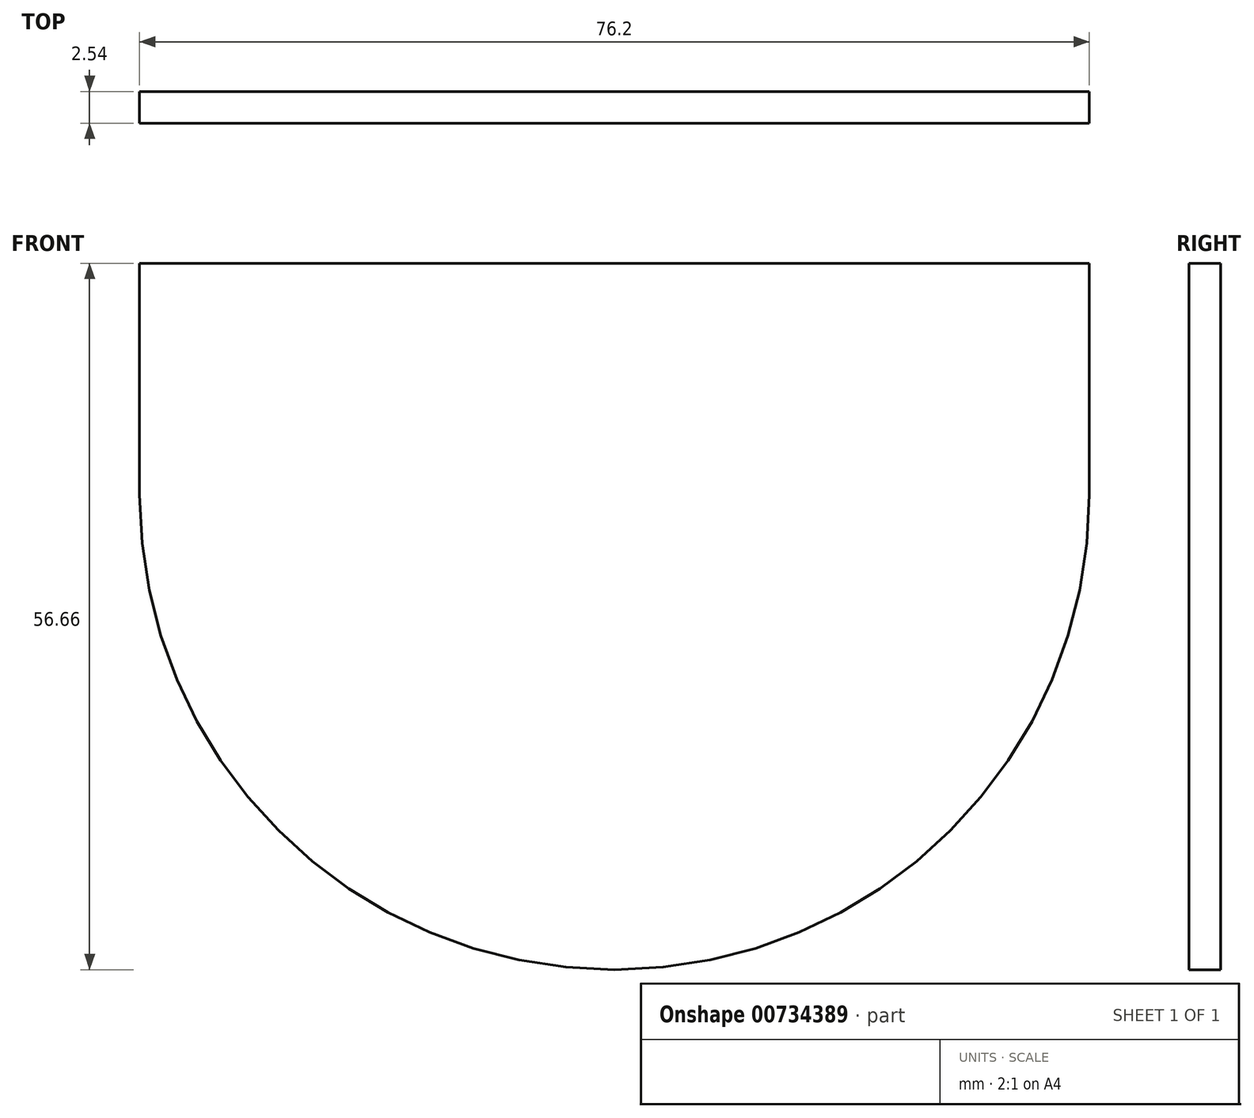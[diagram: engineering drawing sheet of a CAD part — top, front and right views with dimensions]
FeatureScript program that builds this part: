
annotation { "Feature Type Name" : "Feature", "Feature Type Description" : "" }
export const myFeature = defineFeature(function(context is Context, id is Id, definition is map)
    precondition{}
    {
        {
            var Q0;
            Q0=qCreatedBy(makeId("Front.planeOp"),FACE);
            var sketch = newSketch(context, id + "F0", { "sketchPlane" : qUnion([Q0])});
            skLineSegment(sketch, "E0", {"start": v(-47.89, 45.56) * mm, "end": v(28.31, 45.56) * mm});
            skPoint(sketch, "E1", {"position": v(-9.79, 45.56) * mm});
            skLineSegment(sketch, "E2", {"start": v(28.31, 45.56) * mm, "end": v(28.31, 27) * mm});
            skLineSegment(sketch, "E3", {"start": v(-47.89, 45.56) * mm, "end": v(-47.89, 27) * mm});
            skArc(sketch, "E4", {"start": v(-47.89, 27) * mm, "mid": v(-9.79, -11.1) * mm, "end": v(28.31, 27) * mm});
            skSolve(sketch);
        }
        {
            var Q0;
            Q0 = qSketchRegion(id + "F0", true);
            extrude(context, id + "F1", {"entities" : qUnion([Q0]), "depth" : 2.54 * mm, "offsetDistance" : 25.4 * mm});
        }
    });
